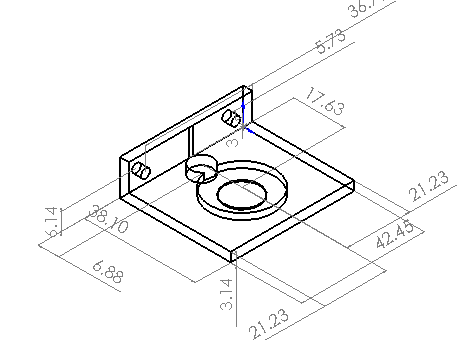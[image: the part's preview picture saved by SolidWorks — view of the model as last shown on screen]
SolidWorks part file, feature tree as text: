
SOLIDWORKS PART (.sldprt)
format: sldprt  version: not decoded by parser v0  size: 232,448 bytes
history: native  units: mm
features: sketch x6, cut_extrude x5, extrude x1 + 1 further entry (+10 scaffold rows collapsed)
feature tree (23):
  "Annotations"  RD1=42.45mm RD2=38.1mm RD3=3.14mm RD4=5.725mm RD5=36.725mm RD6=3mm RD7=6.14mm RD8=21.225mm RD9=21.225mm RD10=6.88mm RD11=17.63mm
  scaffold x10  (default folders/planes/origin — collapsed)
  sketch  "Sketch1"
  extrude  "Extrude1"  Depth=42.45mm
  sketch  "Sketch2"  dims[D1=~1.884375mm]
  cut_extrude  "Cut-Extrude1"  [1 undecoded]
  sketch  "Sketch3"  dims[D1=3.3mm]
  cut_extrude  "Cut-Extrude2"  Depth=2.54mm
  sketch  "Sketch4"  dims[D1=~5.723813mm]
  cut_extrude  "Cut-Extrude3"  Depth=2.14mm
  sketch  "Sketch5"
  cut_extrude  "Cut-Extrude4"  [1 undecoded]
  sketch  "Sketch6"  dims[D1=3.88mm]
  cut_extrude  "Cut-Extrude5"  [1 undecoded]
decode coverage: 7 of 12 modeling features carry decoded parameters; 1 rows unclassified (native names shown)
note: ~ marks probable driven/reference dimensions
note: 3 parameter values undecoded
summary: no parameter record found for 3 features
note: suppression state not decoded; provenance and decode notes live in map.json
